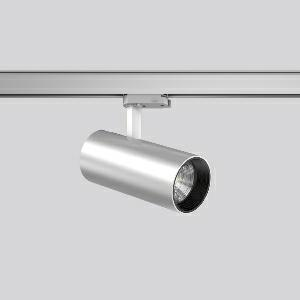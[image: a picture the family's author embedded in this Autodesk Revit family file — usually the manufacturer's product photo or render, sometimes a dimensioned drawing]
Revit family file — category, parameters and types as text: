
# Revit family: deecos_s_mini_742206_004_3_3d4c
name_source: partatom
category: Lighting Fixtures
units: mm (PartAtom-declared; Revit-internal decimal feet)

## family parameters
Cut with Voids When Loaded = No
Host = Face
Light Source = No
Part Type = Normal
Room Calculation Point = No
Round Connector Dimension = Use Diameter
Shared = No

## types (1)
- DEECOS S mini (1 x LED Modul 935, 3250 lm, 3500)
    Apparent Load = 29 VA
    Approval mark = CE
    CIE Flux Codes = 99 100 100 100 100
    Color Rendering = 92
    Color Temperature = 3500
    Default Elevation = 1800 mm
    Description = Series: DEECOS S mini
LED surface-mounted projector in modern design with no visible cooling ribs. Housing: die-cast aluminium, powder-coated. Rotation range: 356°. Swivel range: 90°. Black plastic ring and recessed LED to prevent glare from the side. Optical assembly with lens made of plastic (polycarbonate) for the best homogeneous light distribution - can be changed without tools. Best colour rendering index Ra>90. With multi adaptor for 3-circuit tracks 230 V. Suitable for Track on ceiling, Wall track. High quality converter without flickering and stroboscopic effect. The following accessories can be mounted without use of tools: interchangeable lenses, decorative glasses, honeycomb louvre, clear and frosted diffusers, white interchangeable plastic ring. 
Colour: silver
Diameter: 87 mm
Height: 214 mm
Lamp: LED
Socket: without socket
Colour temperature: 3500K
Colour rendering index (CRI): 92
System power: 29 W
Rated luminous flux: 3250 lm
Luminous efficiency: 112 lm/W
Control gear: Regulated power supply
Protection class: I
Type of protection: IP 20
    Height = 214 mm
    Lamp = 1 x LED Modul 935
    Lamp Light Flux = 3250 lm
    Lamp count = 1
    Length = 87 mm
    Lifetime = 50000 h
    Luminous efficacy = 112 lm/W
    Manufacturer = RZB
    ModVariant = No
    Model = 742206.004.3
    Mounting Place = Ceiling
    Mounting Type = Rail mounted
    Number of Poles = 1
    OnlyDefault = Yes
    Power Factor = 1
    Product Name = DEECOS S mini
    Product group = Track mounted projectors
    ProductGroupID = 301
    Protection Class = Protection class I
    Protection Degree = IP 20
    RLX_Detail_Level = 1
    RLX_Emergency_Light_Flux = 0 lm
    RLX_Emergency_Type = 0
    RLX_Emergency_Type_DB = No
    RlxData = <blob elided: 37537 chars, md5=bfe9ed3c>
    Socket = socket
    Standby Power = 0 W
    System Light Flux = 3250 lm
    System Power = 29 W
    Type Comments = Product without accessories
    Type Image = 741930.004.jpg
    URL = http://relux.com
    VarID = ---
    Voltage = 230 V
    Voltage Range = 220-240 V
    Weight = 0.00 kg
    Width = 0 mm  [stored 0 ft]

note: [stored X ft] marks values corroborated as IEEE doubles in the binary element streams (Revit-internal decimal feet)

## geometry (parser evidence)
native form markers: Blend x4, Sweep x12
no freeform markers — native parametric forms only
